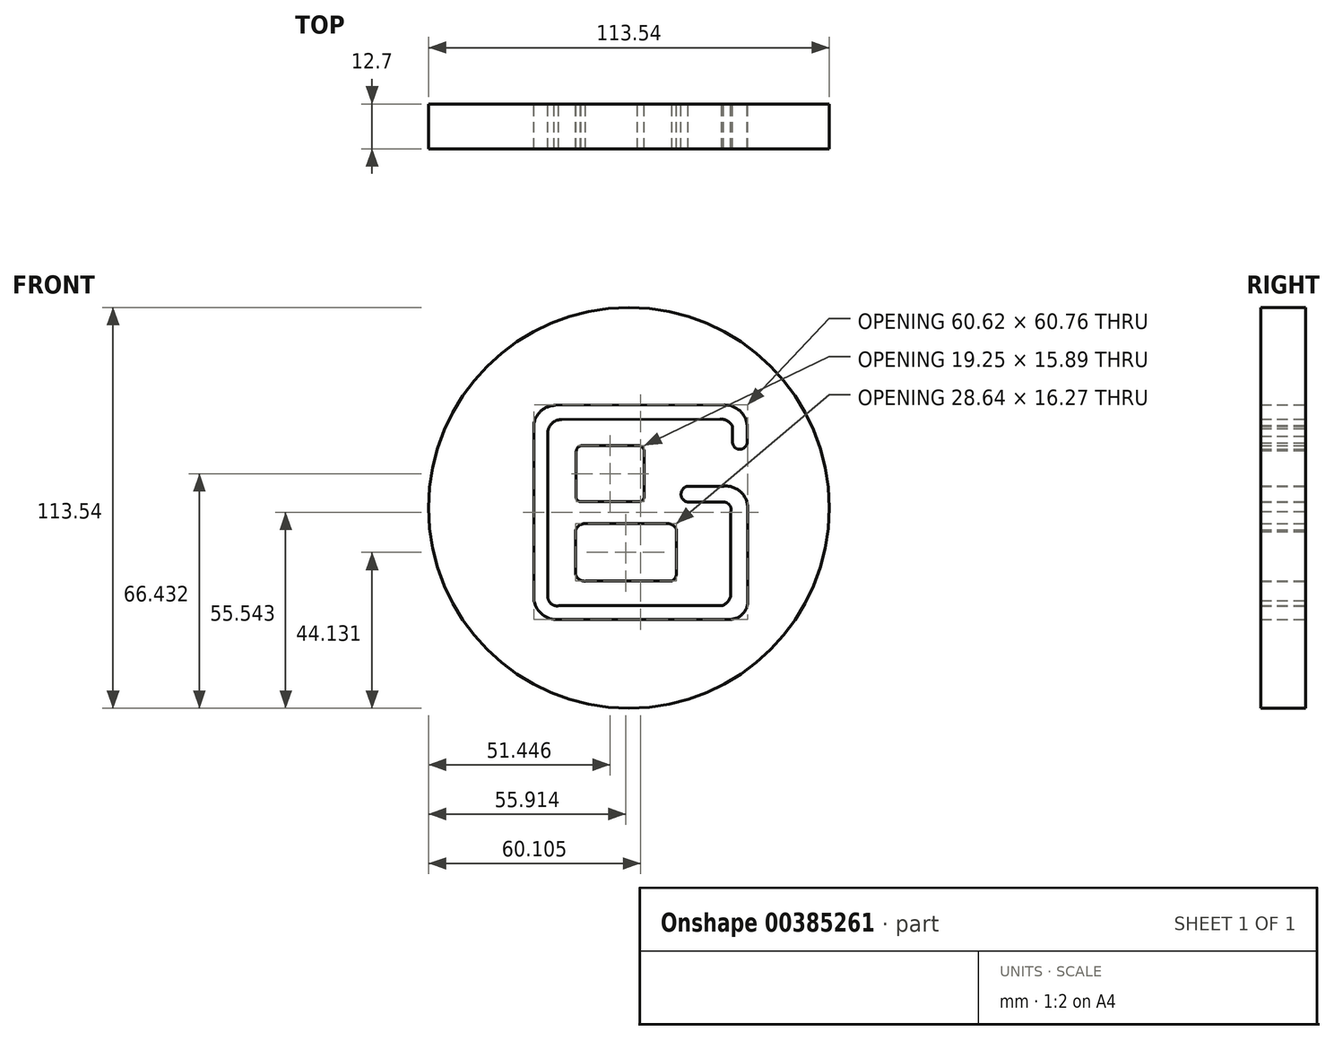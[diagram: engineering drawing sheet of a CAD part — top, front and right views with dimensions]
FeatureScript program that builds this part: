
annotation { "Feature Type Name" : "Feature", "Feature Type Description" : "" }
export const myFeature = defineFeature(function(context is Context, id is Id, definition is map)
    precondition{}
    {
        {
            var Q0;
            Q0=qCreatedBy(makeId("Front.planeOp"),FACE);
            var sketch = newSketch(context, id + "F0", { "sketchPlane" : qUnion([Q0])});
            skLineSegment(sketch, "E0", {"start": v(-20.85, 29.02) * mm, "end": v(27.1, 29.15) * mm});
            skArc(sketch, "E1", {"start": v(-20.85, 29.02) * mm, "mid": v(-25.32, 27.07) * mm, "end": v(-26.98, 22.48) * mm});
            skLineSegment(sketch, "E2", {"start": v(-26.98, 22.48) * mm, "end": v(-26.98, -25.2) * mm});
            skArc(sketch, "E3", {"start": v(-26.98, -25.2) * mm, "mid": v(-25.34, -29.5) * mm, "end": v(-21.26, -31.6) * mm});
            skLineSegment(sketch, "E4", {"start": v(-21.26, -31.6) * mm, "end": v(28.6, -31.6) * mm});
            skArc(sketch, "E5", {"start": v(28.6, -31.6) * mm, "mid": v(32.27, -30.03) * mm, "end": v(33.65, -26.3) * mm});
            skLineSegment(sketch, "E6", {"start": v(33.65, -26.3) * mm, "end": v(33.65, 0) * mm});
            skArc(sketch, "E7", {"start": v(33.65, 0) * mm, "mid": v(31.6, 4.58) * mm, "end": v(26.84, 6.13) * mm});
            skLineSegment(sketch, "E8", {"start": v(26.84, 6.13) * mm, "end": v(17.03, 6.13) * mm});
            skArc(sketch, "E9", {"start": v(17.03, 6.13) * mm, "mid": v(14.77, 4.01) * mm, "end": v(16.75, 1.63) * mm});
            skLineSegment(sketch, "E10", {"start": v(16.75, 1.63) * mm, "end": v(26.84, 1.63) * mm});
            skArc(sketch, "E11", {"start": v(26.84, 1.63) * mm, "mid": v(28.54, 0.78) * mm, "end": v(28.88, -1.1) * mm});
            skLineSegment(sketch, "E12", {"start": v(28.88, -1.1) * mm, "end": v(28.88, -24.25) * mm});
            skArc(sketch, "E13", {"start": v(27.1, 29.15) * mm, "mid": v(31.44, 27.49) * mm, "end": v(33.51, 23.33) * mm});
            skLineSegment(sketch, "E14", {"start": v(33.51, 18.64) * mm, "end": v(33.51, 23.33) * mm});
            skArc(sketch, "E15", {"start": v(33.51, 18.64) * mm, "mid": v(31.56, 16.57) * mm, "end": v(29.39, 18.4) * mm});
            skLineSegment(sketch, "E16", {"start": v(29.39, 18.4) * mm, "end": v(29.39, 23.1) * mm});
            skLineSegment(sketch, "E17", {"start": v(25.84, 25.17) * mm, "end": v(-19.07, 25.04) * mm});
            skArc(sketch, "E18", {"start": v(-19.07, 25.04) * mm, "mid": v(-22.11, 23.6) * mm, "end": v(-22.97, 20.35) * mm});
            skLineSegment(sketch, "E19", {"start": v(-22.97, 20.35) * mm, "end": v(-22.97, -25.2) * mm});
            skArc(sketch, "E20", {"start": v(-22.97, -25.2) * mm, "mid": v(-22.06, -27.17) * mm, "end": v(-19.99, -27.76) * mm});
            skLineSegment(sketch, "E21", {"start": v(-19.99, -27.76) * mm, "end": v(26.3, -27.76) * mm});
            skArc(sketch, "E22", {"start": v(28.88, -24.25) * mm, "mid": v(28.16, -26.43) * mm, "end": v(26.3, -27.76) * mm});
            skArc(sketch, "E23", {"start": v(25.84, 25.17) * mm, "mid": v(27.9, 24.62) * mm, "end": v(29.39, 23.1) * mm});
            skLineSegment(sketch, "E24", {"start": v(-14.95, 15.89) * mm, "end": v(-14.95, 2.94) * mm});
            skArc(sketch, "E25", {"start": v(-14.95, 2.94) * mm, "mid": v(-14.57, 2.09) * mm, "end": v(-13.69, 1.8) * mm});
            skLineSegment(sketch, "E26", {"start": v(-13.69, 1.8) * mm, "end": v(2.35, 1.8) * mm});
            skArc(sketch, "E27", {"start": v(-14.95, 15.89) * mm, "mid": v(-14.56, 16.99) * mm, "end": v(-13.57, 17.6) * mm});
            skLineSegment(sketch, "E28", {"start": v(-13.57, 17.6) * mm, "end": v(2.7, 17.6) * mm});
            skArc(sketch, "E29", {"start": v(2.7, 17.6) * mm, "mid": v(3.75, 17.21) * mm, "end": v(4.3, 16.23) * mm});
            skLineSegment(sketch, "E30", {"start": v(4.3, 16.23) * mm, "end": v(4.3, 3.17) * mm});
            skArc(sketch, "E31", {"start": v(4.3, 3.17) * mm, "mid": v(3.68, 1.98) * mm, "end": v(2.35, 1.8) * mm});
            skLineSegment(sketch, "E32", {"start": v(-12.54, -4.5) * mm, "end": v(11.17, -4.5) * mm});
            skArc(sketch, "E33", {"start": v(11.17, -4.5) * mm, "mid": v(12.6, -4.98) * mm, "end": v(13.46, -6.22) * mm});
            skArc(sketch, "E34", {"start": v(-12.54, -4.5) * mm, "mid": v(-14.29, -5.16) * mm, "end": v(-15.18, -6.8) * mm});
            skLineSegment(sketch, "E35", {"start": v(-15.18, -6.8) * mm, "end": v(-15.18, -18.14) * mm});
            skLineSegment(sketch, "E36", {"start": v(13.46, -6.22) * mm, "end": v(13.46, -18.6) * mm});
            skArc(sketch, "E37", {"start": v(-15.18, -18.14) * mm, "mid": v(-14.32, -20.08) * mm, "end": v(-12.31, -20.77) * mm});
            skLineSegment(sketch, "E38", {"start": v(-12.31, -20.77) * mm, "end": v(12.2, -20.77) * mm});
            skArc(sketch, "E39", {"start": v(13.46, -18.6) * mm, "mid": v(13.13, -19.85) * mm, "end": v(12.2, -20.77) * mm});
            skCircle(sketch, "E40", {"center": v(0, 0) * mm, "radius": 56.77 * mm});
            skCircle(sketch, "E41", {"center": v(0, 0) * mm, "radius": 63.8 * mm});
            skSolve(sketch);
        }
        {
            var Q0;
            Q0=makeQuery(id+"F0.imprint","IMPRINT",FACE,{"disambiguationData":[TD([[makeQuery(id+"F0.imprint","IMPRINT",EDGE,{"derivedFrom":sQuery(id+"F0.wireOp",EDGE,"E0")}),1.0]])]});
            extrude(context, id + "F1", {"entities" : qUnion([Q0]), "endBound" : BoundingType.SYMMETRIC, "depth" : 12.7 * mm, "hasSecondDirectionDraft" : true, "secondDirectionDraftAngle" : 3 * degree});
        }
    });
